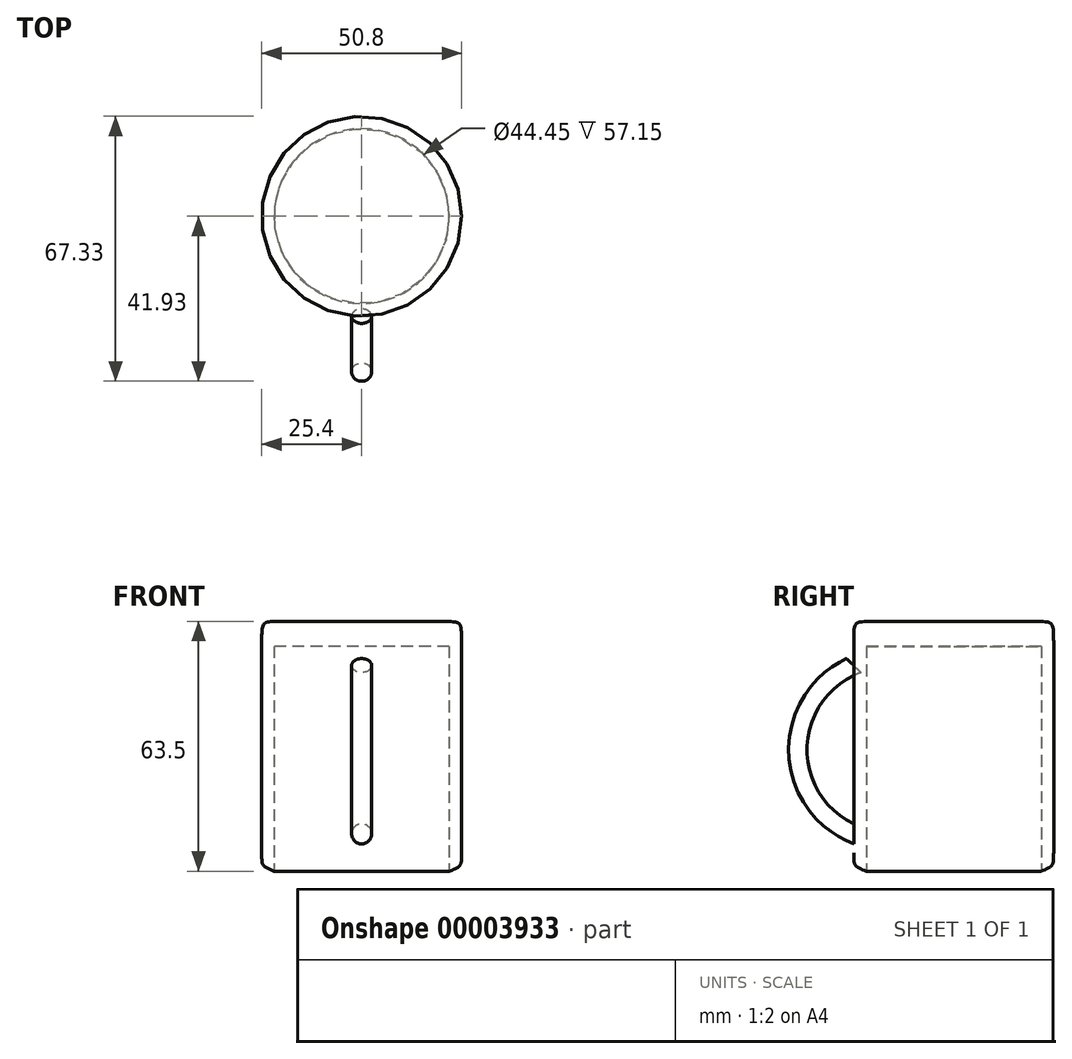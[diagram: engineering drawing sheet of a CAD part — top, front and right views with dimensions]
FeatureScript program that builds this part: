
annotation { "Feature Type Name" : "Feature", "Feature Type Description" : "" }
export const myFeature = defineFeature(function(context is Context, id is Id, definition is map)
    precondition{}
    {
        {
            var Q0;
            Q0=qCreatedBy(makeId("Top.planeOp"),FACE);
            var sketch = newSketch(context, id + "F0", { "sketchPlane" : qUnion([Q0])});
            skCircle(sketch, "E0", {"center": v(0, 0) * mm, "radius": 25.4 * mm});
            skPoint(sketch, "E1", {"position": v(-21.91, 12.85) * mm});
            skSolve(sketch);
        }
        {
            var Q0;
            Q0=makeQuery(id+"F0.imprint","IMPRINT",FACE,{"disambiguationData":[TD([[makeQuery(id+"F0.imprint","IMPRINT",EDGE,{"derivedFrom":sQuery(id+"F0.wireOp",EDGE,"E0")}),1.0]])]});
            extrude(context, id + "F1", {"entities" : qUnion([Q0]), "depth" : 63.5 * mm});
        }
        {
            var Q0;
            Q0=qCreatedBy(makeId("Top.planeOp"),FACE);
            var sketch = newSketch(context, id + "F2", { "sketchPlane" : qUnion([Q0])});
            skCircle(sketch, "E2", {"center": v(0, 0) * mm, "radius": 22.22 * mm});
            skSolve(sketch);
        }
        {
            var Q0;
            Q0=makeQuery(id+"F2.imprint","IMPRINT",FACE,{"disambiguationData":[TD([[makeQuery(id+"F2.imprint","IMPRINT",EDGE,{"derivedFrom":sQuery(id+"F2.wireOp",EDGE,"E2")}),1.0]])]});
            var Q1;
            Q1=makeQuery(id+"F1.opExtrude","CAP_FACE",FACE,{"disambiguationData":[OSD([sQuery(id+"F0.wireOp",EDGE,"E0")])],"isStart":false});
            extrude(context, id + "F3", {"entities" : qUnion([Q0]), "operationType" : NewBodyOperationType.REMOVE, "endBoundEntity" : qUnion([Q1]), "depth" : 57.15 * mm});
        }
        {
            var Q0;
            Q0=makeQuery(id+"F1.opExtrude","CAP_EDGE",EDGE,{"disambiguationData":[OSD([sQuery(id+"F0.wireOp",EDGE,"E0")])],"isStart":true});
            var Q1;
            Q1=makeQuery(id+"F1.opExtrude","CAP_EDGE",EDGE,{"disambiguationData":[OSD([sQuery(id+"F0.wireOp",EDGE,"E0")])],"isStart":false});
            fillet(context, id + "F4", {"entities" : qUnion([Q0, Q1]), "radius" : 5.08 * mm, "tangentPropagation" : true, "rho" : .75, "crossSection" : FilletCrossSection.CONIC, "allowEdgeOverflow" : false});
        }
        {
            var Q0;
            Q0=qCreatedBy(makeId("Front.planeOp"),FACE);
            cPlane(context, id + "F5", {"entities" : qUnion([Q0]), "cplaneType" : CPlaneType.OFFSET, "offset" : 25.4 * mm, "width" : 152.4 * mm, "height" : 152.4 * mm});
        }
        {
            var Q0;
            Q0=qCreatedBy(id+"F5.planeOp",FACE);
            var sketch = newSketch(context, id + "F6", { "sketchPlane" : qUnion([Q0])});
            skCircle(sketch, "E3", {"center": v(0, 9.5) * mm, "radius": 2.54 * mm});
            skCircle(sketch, "E4", {"center": v(0, 52.26) * mm, "radius": 2.54 * mm});
            skSolve(sketch);
        }
        {
            var Q0;
            Q0=qCreatedBy(makeId("Right.planeOp"),FACE);
            var sketch = newSketch(context, id + "F7", { "sketchPlane" : qUnion([Q0])});
            skPoint(sketch, "E5.0", {"position": v(-25.4, 9.5) * mm});
            skPoint(sketch, "E6.0", {"position": v(-25.4, 52.26) * mm});
            skArc(sketch, "E7", {"start": v(-25.4, 52.26) * mm, "mid": v(-39.57, 30.88) * mm, "end": v(-25.4, 9.5) * mm});
            skSolve(sketch);
        }
        {
            var Q0;
            Q0=makeQuery(id+"F6.imprint","IMPRINT",FACE,{"disambiguationData":[TD([[makeQuery(id+"F6.imprint","IMPRINT",EDGE,{"derivedFrom":sQuery(id+"F6.wireOp",EDGE,"E3")}),1.0]])]});
            var Q1;
            Q1=sQuery(id+"F7.wireOp",EDGE,"E7");
            sweep(context, id + "F8", {"profiles" : qUnion([Q0]), "path" : qUnion([Q1])});
        }
    });
